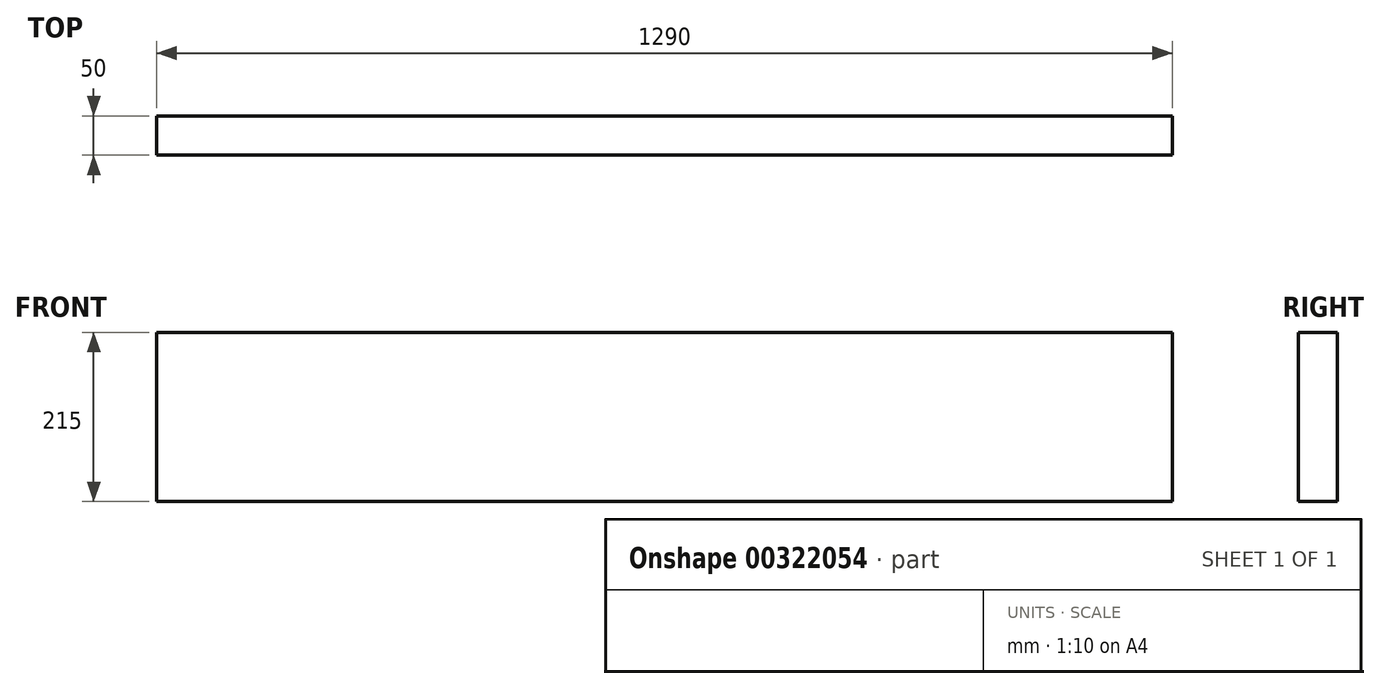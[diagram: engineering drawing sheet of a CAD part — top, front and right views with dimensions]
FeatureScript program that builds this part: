
annotation { "Feature Type Name" : "Feature", "Feature Type Description" : "" }
export const myFeature = defineFeature(function(context is Context, id is Id, definition is map)
    precondition{}
    {
        {
            var Q0;
            Q0=qCreatedBy(makeId("Front.planeOp"),FACE);
            var sketch = newSketch(context, id + "F0", { "sketchPlane" : qUnion([Q0])});
            skLineSegment(sketch, "E0.bottom", {"start": v(645, -107.5) * mm, "end": v(-645, -107.5) * mm});
            skLineSegment(sketch, "E0.top", {"start": v(645, 107.5) * mm, "end": v(-645, 107.5) * mm});
            skLineSegment(sketch, "E0.left", {"start": v(645, -107.5) * mm, "end": v(645, 107.5) * mm});
            skLineSegment(sketch, "E0.right", {"start": v(-645, -107.5) * mm, "end": v(-645, 107.5) * mm});
            skPoint(sketch, "E0.middle", {"position": v(0, 0) * mm});
            skSolve(sketch);
        }
        {
            var Q0;
            Q0=makeQuery(id+"F0.imprint","IMPRINT",FACE,{"disambiguationData":[TD([[makeQuery(id+"F0.imprint","IMPRINT",EDGE,{"derivedFrom":sQuery(id+"F0.wireOp",EDGE,"E0.bottom")}),-1.0]])]});
            extrude(context, id + "F1", {"entities" : qUnion([Q0]), "depth" : 50 * mm});
        }
    });
